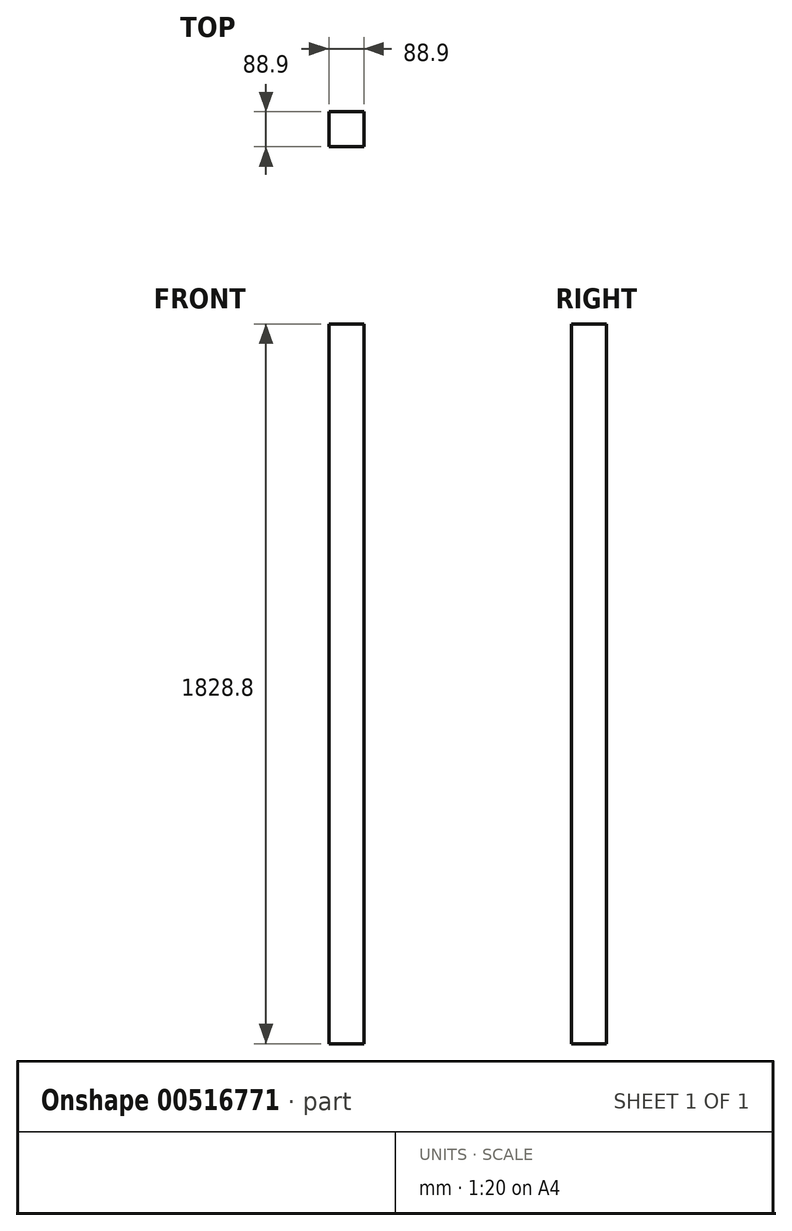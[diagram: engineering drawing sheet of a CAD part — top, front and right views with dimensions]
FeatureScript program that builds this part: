
annotation { "Feature Type Name" : "Feature", "Feature Type Description" : "" }
export const myFeature = defineFeature(function(context is Context, id is Id, definition is map)
    precondition{}
    {
        {
            var Q0;
            Q0=qCreatedBy(makeId("Front.planeOp"),FACE);
            var sketch = newSketch(context, id + "F0", { "sketchPlane" : qUnion([Q0])});
            skLineSegment(sketch, "E0.bottom", {"start": v(0, 0) * mm, "end": v(88.9, 0) * mm});
            skLineSegment(sketch, "E0.top", {"start": v(0, 1828.8) * mm, "end": v(88.9, 1828.8) * mm});
            skLineSegment(sketch, "E0.left", {"start": v(0, 0) * mm, "end": v(0, 1828.8) * mm});
            skLineSegment(sketch, "E0.right", {"start": v(88.9, 0) * mm, "end": v(88.9, 1828.8) * mm});
            skSolve(sketch);
        }
        {
            var Q0;
            Q0=makeQuery(id+"F0.imprint","IMPRINT",FACE,{"disambiguationData":[TD([[makeQuery(id+"F0.imprint","IMPRINT",EDGE,{"derivedFrom":sQuery(id+"F0.wireOp",EDGE,"E0.bottom")}),1.0]])]});
            extrude(context, id + "F1", {"entities" : qUnion([Q0]), "depth" : 88.9 * mm, "offsetDistance" : 25.4 * mm});
        }
    });
